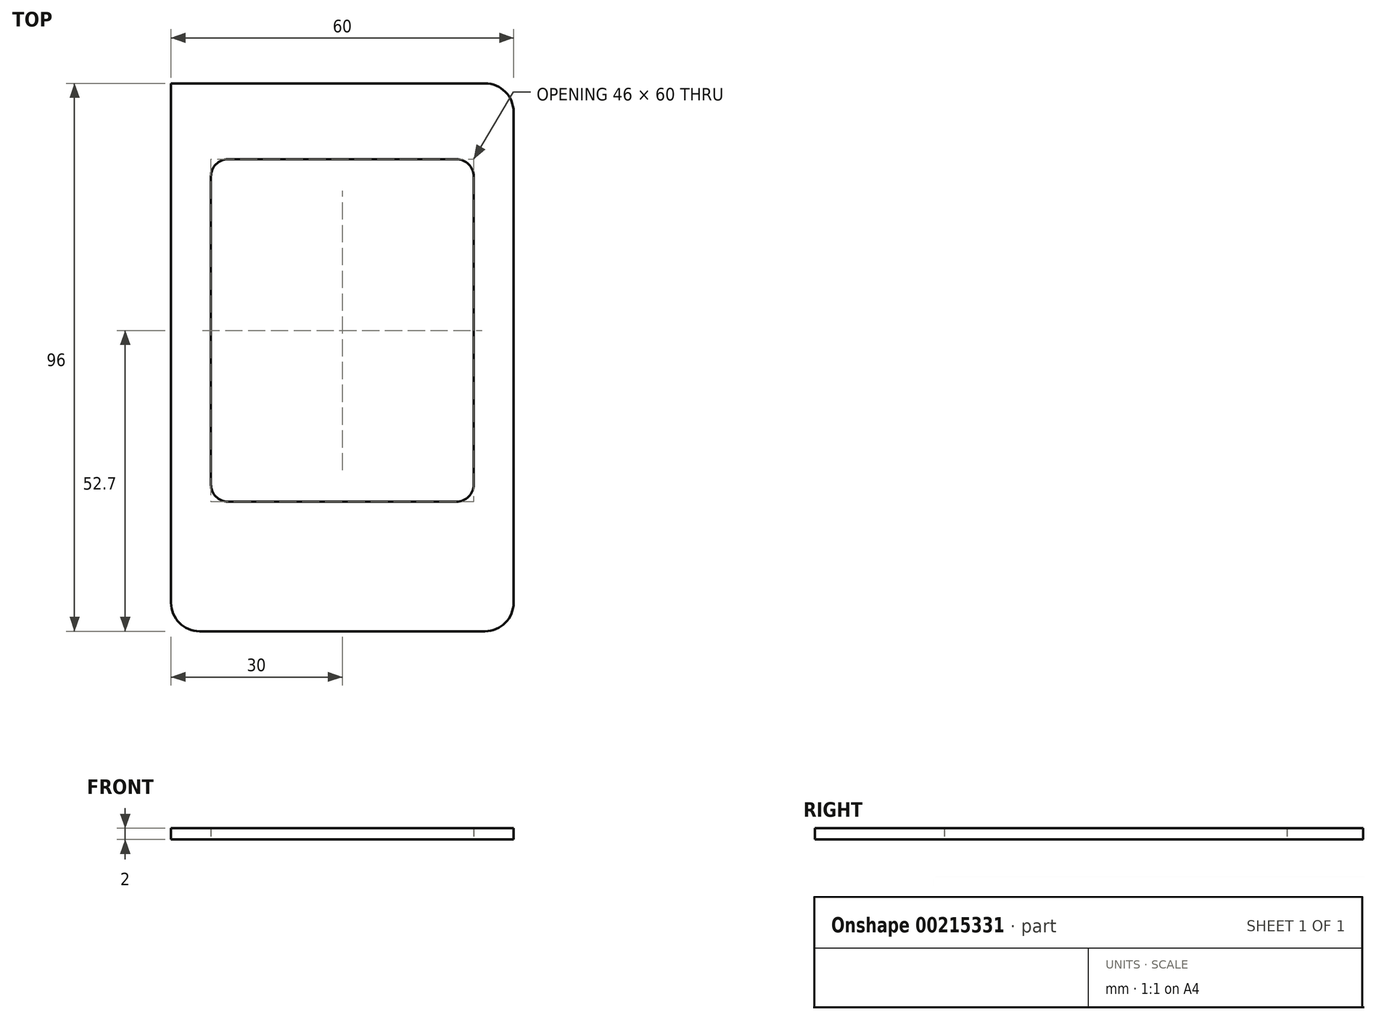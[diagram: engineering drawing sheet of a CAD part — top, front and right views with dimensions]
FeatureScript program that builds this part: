
annotation { "Feature Type Name" : "Feature", "Feature Type Description" : "" }
export const myFeature = defineFeature(function(context is Context, id is Id, definition is map)
    precondition{}
    {
        {
            var Q0;
            Q0=qCreatedBy(makeId("Top.planeOp"),FACE);
            var sketch = newSketch(context, id + "F0", { "sketchPlane" : qUnion([Q0])});
            skPoint(sketch, "E0.middle", {"position": v(0, 0) * mm});
            skLineSegment(sketch, "E1.bottom", {"start": v(25, -48) * mm, "end": v(-25, -48) * mm});
            skLineSegment(sketch, "E1.top", {"start": v(20, 48) * mm, "end": v(-27, 48) * mm});
            skLineSegment(sketch, "E1.left", {"start": v(30, -43) * mm, "end": v(30, 40) * mm});
            skLineSegment(sketch, "E1.right", {"start": v(-30, -43) * mm, "end": v(-30, 43) * mm});
            skLineSegment(sketch, "E2.bottom", {"start": v(-20, 34.7) * mm, "end": v(20, 34.7) * mm});
            skLineSegment(sketch, "E2.top", {"start": v(-20, -25.3) * mm, "end": v(20, -25.3) * mm});
            skLineSegment(sketch, "E2.left", {"start": v(-23, 31.7) * mm, "end": v(-23, -22.3) * mm});
            skLineSegment(sketch, "E2.right", {"start": v(23, 31.7) * mm, "end": v(23, -22.3) * mm});
            skPoint(sketch, "E3.visualSharp", {"position": v(-23, 34.7) * mm});
            skArc(sketch, "E3.filletArc", {"start": v(-20, 34.7) * mm, "mid": v(-22.12, 33.82) * mm, "end": v(-23, 31.7) * mm});
            skPoint(sketch, "E4.visualSharp", {"position": v(23, 34.7) * mm});
            skArc(sketch, "E4.filletArc", {"start": v(23, 31.7) * mm, "mid": v(22.12, 33.82) * mm, "end": v(20, 34.7) * mm});
            skPoint(sketch, "E5.visualSharp", {"position": v(-23, -25.3) * mm});
            skArc(sketch, "E5.filletArc", {"start": v(-23, -22.3) * mm, "mid": v(-22.12, -24.42) * mm, "end": v(-20, -25.3) * mm});
            skPoint(sketch, "E6.visualSharp", {"position": v(23, -25.3) * mm});
            skArc(sketch, "E6.filletArc", {"start": v(20, -25.3) * mm, "mid": v(22.12, -24.42) * mm, "end": v(23, -22.3) * mm});
            skPoint(sketch, "E7.visualSharp", {"position": v(-30, 48) * mm});
            skPoint(sketch, "E8.visualSharp", {"position": v(30, 48) * mm});
            skLineSegment(sketch, "E9.top", {"start": v(-30, 48) * mm, "end": v(-27, 48) * mm});
            skLineSegment(sketch, "E9.left", {"start": v(-30, 43) * mm, "end": v(-30, 48) * mm});
            skPoint(sketch, "E10.visualSharp", {"position": v(-30, -48) * mm});
            skArc(sketch, "E10.filletArc", {"start": v(-30, -43) * mm, "mid": v(-28.54, -46.54) * mm, "end": v(-25, -48) * mm});
            skPoint(sketch, "E11.visualSharp", {"position": v(30, -48) * mm});
            skArc(sketch, "E11.filletArc", {"start": v(25, -48) * mm, "mid": v(28.54, -46.54) * mm, "end": v(30, -43) * mm});
            skLineSegment(sketch, "E12.bottom", {"start": v(20, 48) * mm, "end": v(25, 48) * mm});
            skLineSegment(sketch, "E12.right", {"start": v(30, 43) * mm, "end": v(30, 40) * mm});
            skArc(sketch, "E13.filletArc", {"start": v(30, 43) * mm, "mid": v(28.54, 46.54) * mm, "end": v(25, 48) * mm});
            skSolve(sketch);
        }
        {
            var Q0;
            Q0=qSketchRegion(id+"F0",true);
            extrude(context, id + "F1", {"entities" : qUnion([Q0]), "depth" : 2 * mm});
        }
    });
